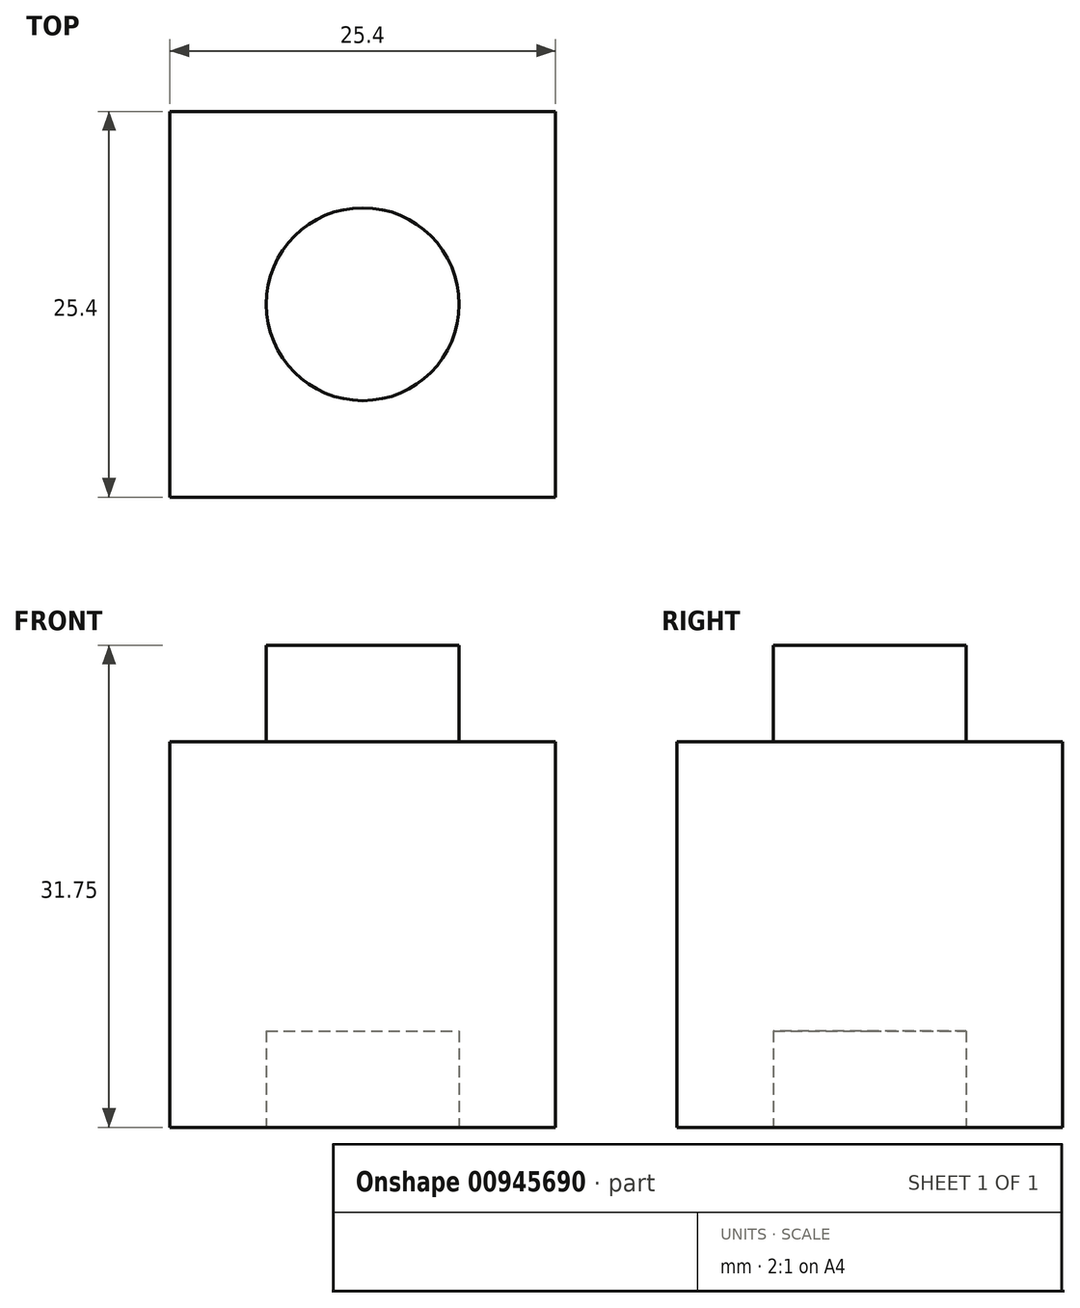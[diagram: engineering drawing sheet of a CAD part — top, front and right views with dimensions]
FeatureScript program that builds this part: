
annotation { "Feature Type Name" : "Feature", "Feature Type Description" : "" }
export const myFeature = defineFeature(function(context is Context, id is Id, definition is map)
    precondition{}
    {
        {
            var Q0;
            Q0=qCreatedBy(makeId("Top.planeOp"),FACE);
            var sketch = newSketch(context, id + "F0", { "sketchPlane" : qUnion([Q0])});
            skLineSegment(sketch, "E0.bottom", {"start": v(12.7, 12.7) * mm, "end": v(-12.7, 12.7) * mm});
            skLineSegment(sketch, "E0.top", {"start": v(12.7, -12.7) * mm, "end": v(-12.7, -12.7) * mm});
            skLineSegment(sketch, "E0.left", {"start": v(12.7, 12.7) * mm, "end": v(12.7, -12.7) * mm});
            skLineSegment(sketch, "E0.right", {"start": v(-12.7, 12.7) * mm, "end": v(-12.7, -12.7) * mm});
            skPoint(sketch, "E0.middle", {"position": v(0, 0) * mm});
            skSolve(sketch);
        }
        {
            var Q0;
            Q0=makeQuery(id+"F0.imprint","IMPRINT",FACE,{"disambiguationData":[TD([[makeQuery(id+"F0.imprint","IMPRINT",EDGE,{"derivedFrom":sQuery(id+"F0.wireOp",EDGE,"E0.bottom")}),1.0]])]});
            extrude(context, id + "F1", {"entities" : qUnion([Q0]), "depth" : 25.4 * mm, "offsetDistance" : 25.4 * mm});
        }
        {
            var Q0;
            Q0=makeQuery(id+"F1.opExtrude","CAP_FACE",FACE,{"disambiguationData":[OSD([sQuery(id+"F0.wireOp",EDGE,"E0.bottom"),sQuery(id+"F0.wireOp",EDGE,"E0.top"),sQuery(id+"F0.wireOp",EDGE,"E0.left"),sQuery(id+"F0.wireOp",EDGE,"E0.right")])],"isStart":true});
            var sketch = newSketch(context, id + "F2", { "sketchPlane" : qUnion([Q0])});
            skCircle(sketch, "E1", {"center": v(0, 0) * mm, "radius": 6.35 * mm});
            skSolve(sketch);
        }
        {
            var Q0;
            Q0=makeQuery(id+"F2.imprint","IMPRINT",FACE,{"disambiguationData":[TD([[makeQuery(id+"F2.imprint","IMPRINT",EDGE,{"derivedFrom":sQuery(id+"F2.wireOp",EDGE,"E1")}),1.0]])]});
            extrude(context, id + "F3", {"entities" : qUnion([Q0]), "operationType" : NewBodyOperationType.REMOVE, "oppositeDirection" : true, "depth" : 6.35 * mm, "offsetDistance" : 25.4 * mm});
        }
        {
            var Q0;
            Q0=makeQuery(id+"F1.opExtrude","CAP_FACE",FACE,{"disambiguationData":[OSD([sQuery(id+"F0.wireOp",EDGE,"E0.bottom"),sQuery(id+"F0.wireOp",EDGE,"E0.top"),sQuery(id+"F0.wireOp",EDGE,"E0.left"),sQuery(id+"F0.wireOp",EDGE,"E0.right")])],"isStart":false});
            var sketch = newSketch(context, id + "F4", { "sketchPlane" : qUnion([Q0])});
            skCircle(sketch, "E2", {"center": v(0, 0) * mm, "radius": 6.35 * mm});
            skSolve(sketch);
        }
        {
            var Q0;
            Q0=makeQuery(id+"F4.imprint","IMPRINT",FACE,{"disambiguationData":[TD([[makeQuery(id+"F4.imprint","IMPRINT",EDGE,{"derivedFrom":sQuery(id+"F4.wireOp",EDGE,"E2")}),1.0]])]});
            extrude(context, id + "F5", {"entities" : qUnion([Q0]), "operationType" : NewBodyOperationType.ADD, "depth" : 6.35 * mm, "offsetDistance" : 25.4 * mm});
        }
    });
